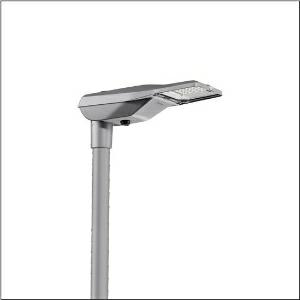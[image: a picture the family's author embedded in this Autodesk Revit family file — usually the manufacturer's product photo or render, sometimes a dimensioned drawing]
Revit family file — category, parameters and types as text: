
# Revit family: streetlight_sl_21_micro___st1_0ab_5xe1m33r08db_c8c0
name_source: partatom
category: Lighting Fixtures
units: mm (PartAtom-declared; Revit-internal decimal feet)

## family parameters
Cut with Voids When Loaded = No
Host = Face
Light Source = No
Part Type = Normal
Room Calculation Point = No
Round Connector Dimension = Use Diameter
Shared = No

## types (1)
- --- (1 x LED, 4500 lm, 39.1 W, 3000K)
    Apparent Load = 39 VA
    CIE Flux Codes = 38 73 97 100 100
    Color Rendering = 70
    Color Temperature = 3000K
    Default Elevation = 1800 mm
    Description = Streetlight SL 21 micro, mast luminaire, primary light control with lens, of PMMA, primary optical cover: cover, of toughened safety glass, transparent, light distribution: ST1.0aB, light emission: direct distribution, primary light characteristic: asymmetric, installation type: side-entry, post-top, LED, High Power LED, rated luminous flux: 4.500lm, luminous efficacy: 115lm/W, light colour: 730, colour temperature: 3000K, control gear: D4i, control: flexible luminous flux parameterisation, time-dependent luminous flux control, constant luminous flux control, overheat protection, pre-setting: logarithmic dimming characteristic, mains connection: 220..240V, AC, 50/60Hz, start of lifetime: 39W, end of service life: 41W, reduction: 18W, luminaire housing, of diecast aluminium, powder-coated, SITECO metallic grey (DB 702S), corrosivity category C5 high according to DIN EN ISO 12944, please order mast flange separately, inclination adjustable: 0°, 5°, 10°, 15°, sealing non-destructively replaceable, multi-level sealing system, length: 528mm, width: 235mm, height: 110mm, mast flange for spigot size: 42mm (side-entry): 5XC10008XM4, 60/48mm (side-entry/post-top): 5XC10108XM2, 76/60mm (side-entry/post-top): 5XC10108XM1, Smart Interface below, protection rating (complete): IP66, insulation class (complete): insulation class II (safety insulation), certification: CE, ENEC, ENEC+, VDE, impact resistance: IK10, permissible operating ambient temperature for outdoor applications: -40..+50°C, standard-compliant lighting for roads and squares, packaging unit: 1 piece

Light Distribution: ST1.0aB
    Height = 110 mm
    Lamp = 1 x LED
    Lamp Light Flux = 4500 lm
    Lamp Power = 39.1 W
    Lamp count = 1
    Length = 528 mm
    Luminous efficacy = 115 lm/W
    Manufacturer = Siteco
    ModVariant = No
    Model = 5XE1M33R08DB
    Number of Poles = 1
    OnlyDefault = Yes
    Power Factor = 1
    Product Name = Streetlight SL 21 micro | ST1.0aB
    Product group = mast luminaire | pylon top
    ProductGroupID = 6100
    Protection Class = Protection class II
    Protection Degree = IP 66
    RLX_Detail_Level = 1
    RLX_Emergency_Light_Flux = 0 lm
    RLX_Emergency_Type = 0
    RLX_Emergency_Type_DB = No
    RlxData = <blob elided: 99077 chars, md5=55c1d0db>
    Socket = socket
    Standby Power = 0 W
    System Light Flux = 4500 lm
    System Power = 39 W
    Type Comments = factory setting: luminous flux: 100 % | dim-lin: 254 | 765 mA
    Type Image = l_1277290.jpg
    URL = http://relux.com
    VarID = @adj_153507
    Voltage = 0 V
    Weight = 0.00 kg
    Width = 235 mm

## geometry (parser evidence)
native form markers: Blend x4, Sweep x10
no freeform markers — native parametric forms only
